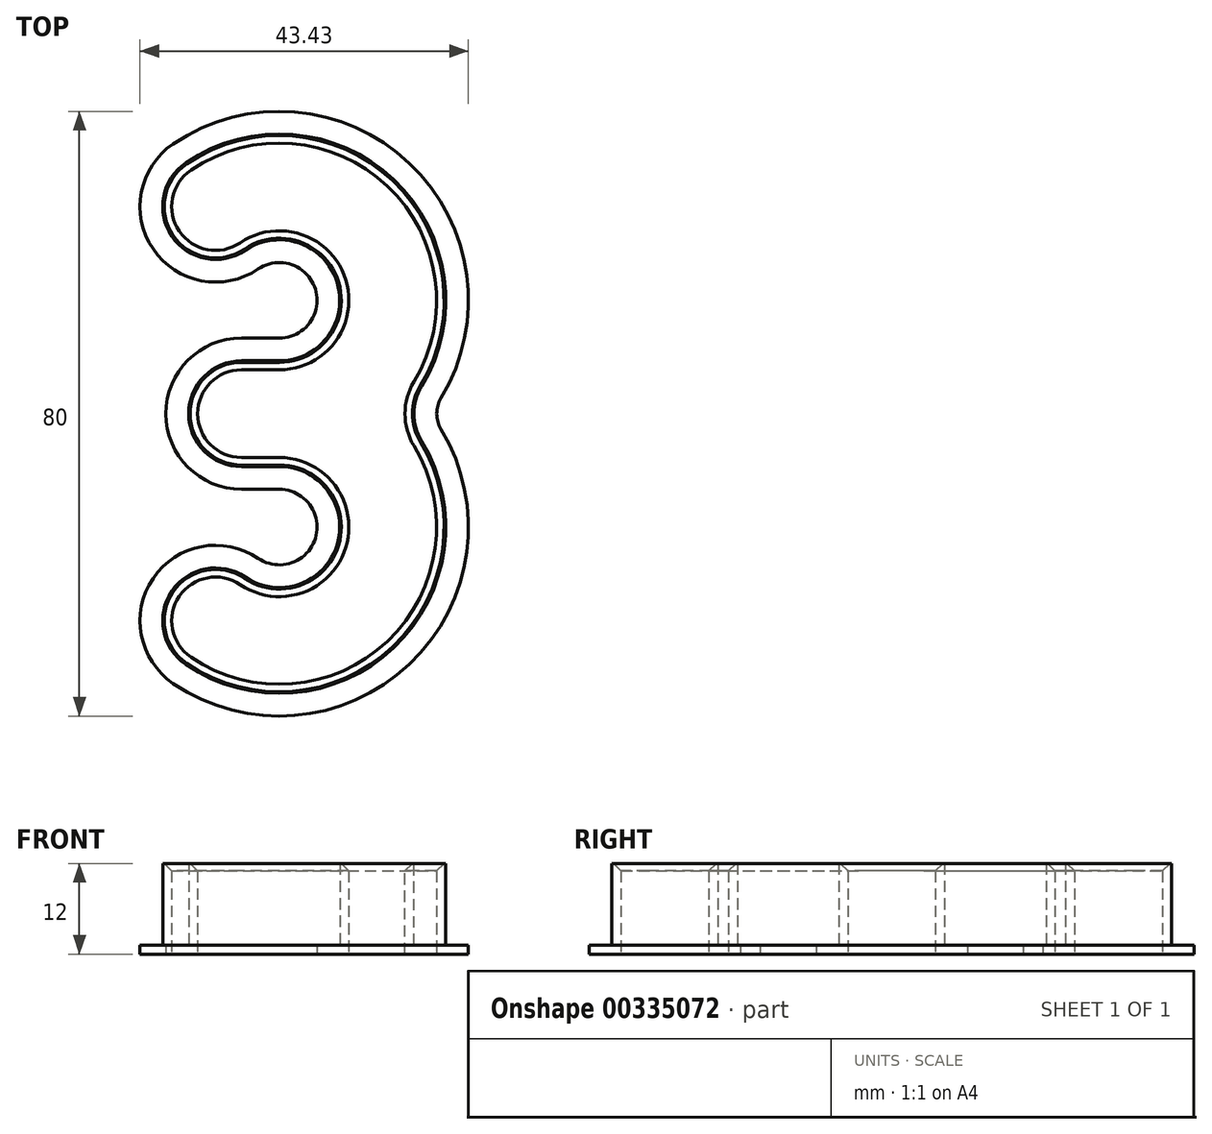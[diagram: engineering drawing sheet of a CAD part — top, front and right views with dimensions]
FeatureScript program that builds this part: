
annotation { "Feature Type Name" : "Feature", "Feature Type Description" : "" }
export const myFeature = defineFeature(function(context is Context, id is Id, definition is map)
    precondition{}
    {
        {
            var Q0;
            Q0=qCreatedBy(makeId("Top.planeOp"),FACE);
            var sketch = newSketch(context, id + "F0", { "sketchPlane" : qUnion([Q0])});
            skArc(sketch, "E0", {"start": v(0, 7) * mm, "mid": v(6.86, 19.12) * mm, "end": v(-7.06, 18.76) * mm});
            skArc(sketch, "E1", {"start": v(-7.06, -18.76) * mm, "mid": v(6.86, -19.12) * mm, "end": v(0, -7) * mm});
            skArc(sketch, "E2", {"start": v(16.1, 0) * mm, "mid": v(12.77, 32.91) * mm, "end": v(-19.42, 25.33) * mm});
            skArc(sketch, "E3", {"start": v(-19.42, -25.33) * mm, "mid": v(12.77, -32.91) * mm, "end": v(16.1, 0) * mm});
            skLineSegment(sketch, "E4", {"start": v(-7.06, 18.76) * mm, "end": v(-19.42, 25.33) * mm});
            skLineSegment(sketch, "E5.MirrorCS", {"start": v(-7.06, -18.76) * mm, "end": v(-19.42, -25.33) * mm});
            skLineSegment(sketch, "E6", {"start": v(0, 7) * mm, "end": v(-12, 7) * mm});
            skLineSegment(sketch, "E7", {"start": v(0, -7) * mm, "end": v(-12, -7) * mm});
            skLineSegment(sketch, "E8", {"start": v(-12, 7) * mm, "end": v(-12, -7) * mm});
            skSolve(sketch);
        }
        {
            var Q0;
            Q0 = qSketchRegion(id + "F0", true);
            extrude(context, id + "F1", {"entities" : qUnion([Q0]), "depth" : 12 * mm});
        }
        {
            var Q0;
            Q0=makeQuery(id+"F1.opExtrude","SWEPT_EDGE",EDGE,{"disambiguationData":[OSD([sQuery(id+"F0.wireOp",EDGE,"E2"),sQuery(id+"F0.wireOp",EDGE,"E4")])]});
            var Q1;
            Q1=makeQuery(id+"F1.opExtrude","SWEPT_EDGE",EDGE,{"disambiguationData":[OSD([sQuery(id+"F0.wireOp",EDGE,"E0"),sQuery(id+"F0.wireOp",EDGE,"E4")])]});
            var Q2;
            Q2=makeQuery(id+"F1.opExtrude","SWEPT_EDGE",EDGE,{"disambiguationData":[OSD([sQuery(id+"F0.wireOp",EDGE,"E6"),sQuery(id+"F0.wireOp",EDGE,"E8")])]});
            var Q3;
            Q3=makeQuery(id+"F1.opExtrude","SWEPT_EDGE",EDGE,{"disambiguationData":[OSD([sQuery(id+"F0.wireOp",EDGE,"E7"),sQuery(id+"F0.wireOp",EDGE,"E8")])]});
            var Q4;
            Q4=makeQuery(id+"F1.opExtrude","SWEPT_EDGE",EDGE,{"disambiguationData":[OSD([sQuery(id+"F0.wireOp",EDGE,"E1"),sQuery(id+"F0.wireOp",EDGE,"E5.MirrorCS")])]});
            var Q5;
            Q5=makeQuery(id+"F1.opExtrude","SWEPT_EDGE",EDGE,{"disambiguationData":[OSD([sQuery(id+"F0.wireOp",EDGE,"E3"),sQuery(id+"F0.wireOp",EDGE,"E5.MirrorCS")])]});
            var Q6;
            Q6=makeQuery(id+"F1.opExtrude","SWEPT_EDGE",EDGE,{"disambiguationData":[OSD([sQuery(id+"F0.wireOp",EDGE,"E2"),sQuery(id+"F0.wireOp",EDGE,"E3")])]});
            fillet(context, id + "F2", {"entities" : qUnion([Q0, Q1, Q2, Q3, Q4, Q5, Q6]), "radius" : 7 * mm, "tangentPropagation" : true, "allowEdgeOverflow" : false});
        }
        {
            var Q0;
            Q0=makeQuery(id+"F1.opExtrude","CAP_FACE",FACE,{"disambiguationData":[OSD([sQuery(id+"F0.wireOp",EDGE,"E0"),sQuery(id+"F0.wireOp",EDGE,"E1"),sQuery(id+"F0.wireOp",EDGE,"E2"),sQuery(id+"F0.wireOp",EDGE,"E3"),sQuery(id+"F0.wireOp",EDGE,"E4"),sQuery(id+"F0.wireOp",EDGE,"E5.MirrorCS"),sQuery(id+"F0.wireOp",EDGE,"E6"),sQuery(id+"F0.wireOp",EDGE,"E7"),sQuery(id+"F0.wireOp",EDGE,"E8")])],"isStart":false});
            var Q1;
            Q1=makeQuery(id+"F1.opExtrude","CAP_FACE",FACE,{"disambiguationData":[OSD([sQuery(id+"F0.wireOp",EDGE,"E0"),sQuery(id+"F0.wireOp",EDGE,"E1"),sQuery(id+"F0.wireOp",EDGE,"E2"),sQuery(id+"F0.wireOp",EDGE,"E3"),sQuery(id+"F0.wireOp",EDGE,"E4"),sQuery(id+"F0.wireOp",EDGE,"E5.MirrorCS"),sQuery(id+"F0.wireOp",EDGE,"E6"),sQuery(id+"F0.wireOp",EDGE,"E7"),sQuery(id+"F0.wireOp",EDGE,"E8")])],"isStart":true});
            shell(context, id + "F3", {"entities" : qUnion([Q0, Q1]), "thickness" : 1.2 * mm});
        }
        {
            var Q0;
            Q0=makeQuery(id+"F1.opExtrude","CAP_FACE",FACE,{"disambiguationData":[OSD([sQuery(id+"F0.wireOp",EDGE,"E0"),sQuery(id+"F0.wireOp",EDGE,"E1"),sQuery(id+"F0.wireOp",EDGE,"E2"),sQuery(id+"F0.wireOp",EDGE,"E3"),sQuery(id+"F0.wireOp",EDGE,"E4"),sQuery(id+"F0.wireOp",EDGE,"E5.MirrorCS"),sQuery(id+"F0.wireOp",EDGE,"E6"),sQuery(id+"F0.wireOp",EDGE,"E7"),sQuery(id+"F0.wireOp",EDGE,"E8")])],"isStart":true});
            var sketch = newSketch(context, id + "F4", { "sketchPlane" : qUnion([Q0])});
            skArc(sketch, "E9.0", {"start": v(-12.36, 33.2) * mm, "mid": v(-14.22, 23.48) * mm, "end": v(-4.5, 21.62) * mm});
            skArc(sketch, "E10.0", {"start": v(-12.36, 33.2) * mm, "mid": v(15.14, 30.96) * mm, "end": v(18.83, 3.62) * mm});
            skArc(sketch, "E11.0", {"start": v(18.83, -3.62) * mm, "mid": v(17.82, 0) * mm, "end": v(18.83, 3.62) * mm});
            skArc(sketch, "E12.0", {"start": v(18.83, -3.62) * mm, "mid": v(15.14, -30.96) * mm, "end": v(-12.36, -33.2) * mm});
            skArc(sketch, "E13.0", {"start": v(-4.5, -21.62) * mm, "mid": v(-14.22, -23.48) * mm, "end": v(-12.36, -33.2) * mm});
            skArc(sketch, "E14.0", {"start": v(0, -7) * mm, "mid": v(7.65, -17.35) * mm, "end": v(-4.5, -21.62) * mm});
            skLineSegment(sketch, "E15.0", {"start": v(0, -7) * mm, "end": v(-5, -7) * mm});
            skArc(sketch, "E16.0", {"start": v(-5, 7) * mm, "mid": v(-12, 0) * mm, "end": v(-5, -7) * mm});
            skLineSegment(sketch, "E17.0", {"start": v(0, 7) * mm, "end": v(-5, 7) * mm});
            skArc(sketch, "E18.0", {"start": v(-4.5, 21.62) * mm, "mid": v(7.65, 17.35) * mm, "end": v(0, 7) * mm});
            skArc(sketch, "E19.0", {"start": v(-14.05, 35.68) * mm, "mid": v(17.2, 33.14) * mm, "end": v(21.4, 2.07) * mm});
            skArc(sketch, "E19.1", {"start": v(21.4, -2.07) * mm, "mid": v(20.82, 0) * mm, "end": v(21.4, 2.07) * mm});
            skArc(sketch, "E19.2", {"start": v(-14.05, 35.68) * mm, "mid": v(-16.7, 21.8) * mm, "end": v(-2.8, 19.14) * mm});
            skArc(sketch, "E19.3", {"start": v(21.4, -2.07) * mm, "mid": v(17.2, -33.14) * mm, "end": v(-14.05, -35.68) * mm});
            skArc(sketch, "E19.4", {"start": v(-2.8, -19.14) * mm, "mid": v(-16.7, -21.8) * mm, "end": v(-14.05, -35.68) * mm});
            skArc(sketch, "E19.5", {"start": v(0, -10) * mm, "mid": v(4.78, -16.47) * mm, "end": v(-2.8, -19.14) * mm});
            skArc(sketch, "E19.6", {"start": v(-2.8, 19.14) * mm, "mid": v(4.78, 16.47) * mm, "end": v(0, 10) * mm});
            skLineSegment(sketch, "E19.7", {"start": v(0, 10) * mm, "end": v(-5, 10) * mm});
            skArc(sketch, "E19.8", {"start": v(-5, 10) * mm, "mid": v(-15, 0) * mm, "end": v(-5, -10) * mm});
            skLineSegment(sketch, "E19.9", {"start": v(0, -10) * mm, "end": v(-5, -10) * mm});
            skSolve(sketch);
        }
        {
            var Q0;
            Q0 = qSketchRegion(id + "F4", true);
            extrude(context, id + "F5", {"entities" : qUnion([Q0]), "operationType" : NewBodyOperationType.ADD, "oppositeDirection" : true, "depth" : 1.2 * mm});
        }
        {
            var Q0;
            {var subQ0=sQuery(id+"F0.wireOp",EDGE,"E0");Q0=makeQuery(id+"F3.opShell","OFFSET_EDGE",EDGE,{"disambiguationData":[OSD([subQ0]),TDD([makeQuery(id+"F1.opExtrude","CAP_EDGE",EDGE,{"disambiguationData":[OSD([subQ0])],"isStart":false})])]});}
            chamfer(context, id + "F6", {"entities" : qUnion([Q0]), "width" : 1 * mm, "tangentPropagation" : true});
        }
    });
